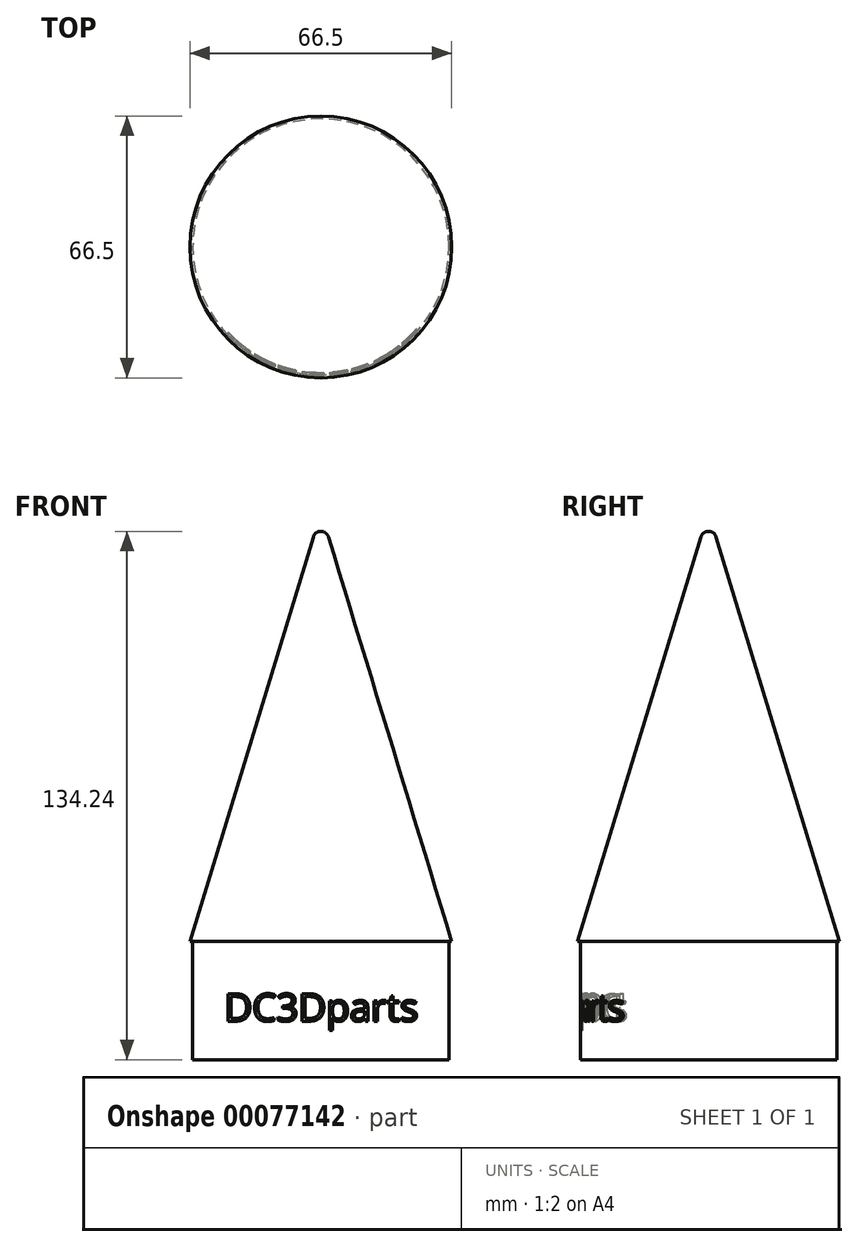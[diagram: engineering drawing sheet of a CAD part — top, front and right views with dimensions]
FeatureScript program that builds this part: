
annotation { "Feature Type Name" : "Feature", "Feature Type Description" : "" }
export const myFeature = defineFeature(function(context is Context, id is Id, definition is map)
    precondition{}
    {
        {
            var Q0;
            Q0=qCreatedBy(makeId("Front.planeOp"),FACE);
            var sketch = newSketch(context, id + "F0", { "sketchPlane" : qUnion([Q0])});
            skLineSegment(sketch, "E0", {"start": v(0, 91.38) * mm, "end": v(0, -88.55) * mm, "construction": true});
            skPoint(sketch, "E0.startSnap0", {"position": v(0, 78.7) * mm});
            skLineSegment(sketch, "E1", {"start": v(-62.51, 0) * mm, "end": v(-32.55, 0) * mm, "construction": true});
            skLineSegment(sketch, "E2.top", {"start": v(0, -30) * mm, "end": v(-32.55, -30) * mm});
            skLineSegment(sketch, "E2.left", {"start": v(0, 0) * mm, "end": v(0, -30) * mm});
            skLineSegment(sketch, "E2.right", {"start": v(-32.55, 0) * mm, "end": v(-32.55, -30) * mm});
            skLineSegment(sketch, "E3", {"start": v(0, 78.7) * mm, "end": v(0, -30) * mm});
            skLineSegment(sketch, "E4.trimOffspring", {"start": v(0, 0) * mm, "end": v(63.8, 0) * mm, "construction": true});
            skLineSegment(sketch, "E5", {"start": v(-33.25, 0) * mm, "end": v(-32.55, 0) * mm});
            skLineSegment(sketch, "E6", {"start": v(-33.25, 0) * mm, "end": v(-1.92, 102.82) * mm});
            skLineSegment(sketch, "E7", {"start": v(0, 104.24) * mm, "end": v(0, -30) * mm});
            skArc(sketch, "E8", {"start": v(0, 104.24) * mm, "mid": v(-1.2, 103.85) * mm, "end": v(-1.92, 102.82) * mm});
            skPoint(sketch, "E9.orphan", {"position": v(0, 109.12) * mm});
            skSolve(sketch);
        }
        {
            var Q0;
            {var subQ0=sQuery(id+"F0.wireOp",EDGE,"E2.top");Q0=makeQuery(id+"F0.imprint","IMPRINT",FACE,{"disambiguationData":[TD([[makeQuery(id+"F0.imprint","IMPRINT",EDGE,{"derivedFrom":subQ0}),-1.0]])]});}
            var Q1;
            Q1=sQuery(id+"F0.wireOp",EDGE,"E0");
            revolve(context, id + "F1", {"entities" : qUnion([Q0]), "axis" : qUnion([Q1]), "revolveType" : RevolveType.FULL});
        }
        {
            var Q0;
            Q0=qCreatedBy(makeId("Front.planeOp"),FACE);
            cPlane(context, id + "F2", {"entities" : qUnion([Q0]), "cplaneType" : CPlaneType.OFFSET, "offset" : 40 * mm, "width" : 150 * mm, "height" : 150 * mm});
        }
        {
            var Q0;
            Q0=qCreatedBy(id+"F2.planeOp",FACE);
            var sketch = newSketch(context, id + "F3", { "sketchPlane" : qUnion([Q0])});
            skText(sketch, "E10", { "text": "DC3Dparts", "fontName": "OpenSans-Regular.ttf"});
            const initialGuessF3  = {"E10": [-0.02452, -0.02022, 1, 0, 0.007]};
            skSetInitialGuess(sketch, initialGuessF3);
            skSolve(sketch);
        }
        {
            var Q0;
            Q0 = qSketchRegion(id + "F3", true);
            var Q1;
            Q1=qCreatedBy(makeId("Front.planeOp"),FACE);
            extrude(context, id + "F4", {"entities" : qUnion([Q0]), "endBound" : BoundingType.UP_TO_SURFACE, "oppositeDirection" : true, "depth" : 25 * mm, "endBoundEntityFace" : qUnion([Q1]), "offsetDistance" : 25 * mm});
        }
        {
            var Q0;
            Q0=qCreatedBy(makeId("Front.planeOp"),FACE);
            var sketch = newSketch(context, id + "F5", { "sketchPlane" : qUnion([Q0])});
            skLineSegment(sketch, "E11.bottom", {"start": v(0, -2.97) * mm, "end": v(-32, -2.97) * mm});
            skLineSegment(sketch, "E11.top", {"start": v(0, -33.64) * mm, "end": v(-32, -33.64) * mm});
            skLineSegment(sketch, "E11.left", {"start": v(0, -2.97) * mm, "end": v(0, -33.64) * mm});
            skLineSegment(sketch, "E11.right", {"start": v(-32, -2.97) * mm, "end": v(-32, -33.64) * mm});
            skSolve(sketch);
        }
        {
            var Q0;
            Q0=makeQuery(id+"F5.imprint","IMPRINT",FACE,{"disambiguationData":[TD([[makeQuery(id+"F5.imprint","IMPRINT",EDGE,{"derivedFrom":sQuery(id+"F5.wireOp",EDGE,"E11.bottom")}),1.0]])]});
            var Q1;
            Q1=sQuery(id+"F5.wireOp",EDGE,"E11.left");
            revolve(context, id + "F6", {"entities" : qUnion([Q0]), "axis" : qUnion([Q1]), "revolveType" : RevolveType.FULL});
        }
        {
            var Q0;
            Q0=makeQuery(id+"F6.opRevolve","SWEPT_BODY",BODY,{"disambiguationData":[OSD([sQuery(id+"F5.wireOp",EDGE,"E11.bottom"),sQuery(id+"F5.wireOp",EDGE,"E11.top"),sQuery(id+"F5.wireOp",EDGE,"E11.left"),sQuery(id+"F5.wireOp",EDGE,"E11.right")])]});
            var Q1;
            Q1=makeQuery(id+"F4.opExtrude","SWEPT_BODY",BODY,{"disambiguationData":[OSD([sQuery(id+"F3.wireOp",EDGE,"E10.sketch_text.stroke-0"),sQuery(id+"F3.wireOp",EDGE,"E10.sketch_text.stroke-1"),sQuery(id+"F3.wireOp",EDGE,"E10.sketch_text.stroke-2"),sQuery(id+"F3.wireOp",EDGE,"E10.sketch_text.stroke-3"),sQuery(id+"F3.wireOp",EDGE,"E10.sketch_text.stroke-4"),sQuery(id+"F3.wireOp",EDGE,"E10.sketch_text.stroke-5"),sQuery(id+"F3.wireOp",EDGE,"E10.sketch_text.stroke-6"),sQuery(id+"F3.wireOp",EDGE,"E10.sketch_text.stroke-7"),sQuery(id+"F3.wireOp",EDGE,"E10.sketch_text.stroke-8"),sQuery(id+"F3.wireOp",EDGE,"E10.sketch_text.stroke-9"),sQuery(id+"F3.wireOp",EDGE,"E10.sketch_text.stroke-10"),sQuery(id+"F3.wireOp",EDGE,"E10.sketch_text.stroke-11"),sQuery(id+"F3.wireOp",EDGE,"E10.sketch_text.stroke-12"),sQuery(id+"F3.wireOp",EDGE,"E10.sketch_text.stroke-13")])]});
            var Q2;
            Q2=makeQuery(id+"F4.opExtrude","SWEPT_BODY",BODY,{"disambiguationData":[OSD([sQuery(id+"F3.wireOp",EDGE,"E10.sketch_text.stroke-14"),sQuery(id+"F3.wireOp",EDGE,"E10.sketch_text.stroke-15"),sQuery(id+"F3.wireOp",EDGE,"E10.sketch_text.stroke-16"),sQuery(id+"F3.wireOp",EDGE,"E10.sketch_text.stroke-17"),sQuery(id+"F3.wireOp",EDGE,"E10.sketch_text.stroke-18"),sQuery(id+"F3.wireOp",EDGE,"E10.sketch_text.stroke-19"),sQuery(id+"F3.wireOp",EDGE,"E10.sketch_text.stroke-20"),sQuery(id+"F3.wireOp",EDGE,"E10.sketch_text.stroke-21"),sQuery(id+"F3.wireOp",EDGE,"E10.sketch_text.stroke-22"),sQuery(id+"F3.wireOp",EDGE,"E10.sketch_text.stroke-23"),sQuery(id+"F3.wireOp",EDGE,"E10.sketch_text.stroke-24"),sQuery(id+"F3.wireOp",EDGE,"E10.sketch_text.stroke-25"),sQuery(id+"F3.wireOp",EDGE,"E10.sketch_text.stroke-26"),sQuery(id+"F3.wireOp",EDGE,"E10.sketch_text.stroke-27"),sQuery(id+"F3.wireOp",EDGE,"E10.sketch_text.stroke-28")])]});
            var Q3;
            Q3=makeQuery(id+"F4.opExtrude","SWEPT_BODY",BODY,{"disambiguationData":[OSD([sQuery(id+"F3.wireOp",EDGE,"E10.sketch_text.stroke-29"),sQuery(id+"F3.wireOp",EDGE,"E10.sketch_text.stroke-30"),sQuery(id+"F3.wireOp",EDGE,"E10.sketch_text.stroke-31"),sQuery(id+"F3.wireOp",EDGE,"E10.sketch_text.stroke-32"),sQuery(id+"F3.wireOp",EDGE,"E10.sketch_text.stroke-33"),sQuery(id+"F3.wireOp",EDGE,"E10.sketch_text.stroke-34"),sQuery(id+"F3.wireOp",EDGE,"E10.sketch_text.stroke-35"),sQuery(id+"F3.wireOp",EDGE,"E10.sketch_text.stroke-36"),sQuery(id+"F3.wireOp",EDGE,"E10.sketch_text.stroke-37"),sQuery(id+"F3.wireOp",EDGE,"E10.sketch_text.stroke-38"),sQuery(id+"F3.wireOp",EDGE,"E10.sketch_text.stroke-39"),sQuery(id+"F3.wireOp",EDGE,"E10.sketch_text.stroke-40"),sQuery(id+"F3.wireOp",EDGE,"E10.sketch_text.stroke-41"),sQuery(id+"F3.wireOp",EDGE,"E10.sketch_text.stroke-42"),sQuery(id+"F3.wireOp",EDGE,"E10.sketch_text.stroke-43"),sQuery(id+"F3.wireOp",EDGE,"E10.sketch_text.stroke-44"),sQuery(id+"F3.wireOp",EDGE,"E10.sketch_text.stroke-45"),sQuery(id+"F3.wireOp",EDGE,"E10.sketch_text.stroke-46"),sQuery(id+"F3.wireOp",EDGE,"E10.sketch_text.stroke-47"),sQuery(id+"F3.wireOp",EDGE,"E10.sketch_text.stroke-48"),sQuery(id+"F3.wireOp",EDGE,"E10.sketch_text.stroke-49"),sQuery(id+"F3.wireOp",EDGE,"E10.sketch_text.stroke-50"),sQuery(id+"F3.wireOp",EDGE,"E10.sketch_text.stroke-51"),sQuery(id+"F3.wireOp",EDGE,"E10.sketch_text.stroke-52"),sQuery(id+"F3.wireOp",EDGE,"E10.sketch_text.stroke-53"),sQuery(id+"F3.wireOp",EDGE,"E10.sketch_text.stroke-54"),sQuery(id+"F3.wireOp",EDGE,"E10.sketch_text.stroke-55"),sQuery(id+"F3.wireOp",EDGE,"E10.sketch_text.stroke-56")])]});
            var Q4;
            Q4=makeQuery(id+"F4.opExtrude","SWEPT_BODY",BODY,{"disambiguationData":[OSD([sQuery(id+"F3.wireOp",EDGE,"E10.sketch_text.stroke-57"),sQuery(id+"F3.wireOp",EDGE,"E10.sketch_text.stroke-58"),sQuery(id+"F3.wireOp",EDGE,"E10.sketch_text.stroke-59"),sQuery(id+"F3.wireOp",EDGE,"E10.sketch_text.stroke-60"),sQuery(id+"F3.wireOp",EDGE,"E10.sketch_text.stroke-61"),sQuery(id+"F3.wireOp",EDGE,"E10.sketch_text.stroke-62"),sQuery(id+"F3.wireOp",EDGE,"E10.sketch_text.stroke-63"),sQuery(id+"F3.wireOp",EDGE,"E10.sketch_text.stroke-64"),sQuery(id+"F3.wireOp",EDGE,"E10.sketch_text.stroke-65"),sQuery(id+"F3.wireOp",EDGE,"E10.sketch_text.stroke-66"),sQuery(id+"F3.wireOp",EDGE,"E10.sketch_text.stroke-67"),sQuery(id+"F3.wireOp",EDGE,"E10.sketch_text.stroke-68"),sQuery(id+"F3.wireOp",EDGE,"E10.sketch_text.stroke-69"),sQuery(id+"F3.wireOp",EDGE,"E10.sketch_text.stroke-70")])]});
            var Q5;
            Q5=makeQuery(id+"F4.opExtrude","SWEPT_BODY",BODY,{"disambiguationData":[OSD([sQuery(id+"F3.wireOp",EDGE,"E10.sketch_text.stroke-71"),sQuery(id+"F3.wireOp",EDGE,"E10.sketch_text.stroke-72"),sQuery(id+"F3.wireOp",EDGE,"E10.sketch_text.stroke-73"),sQuery(id+"F3.wireOp",EDGE,"E10.sketch_text.stroke-74"),sQuery(id+"F3.wireOp",EDGE,"E10.sketch_text.stroke-75"),sQuery(id+"F3.wireOp",EDGE,"E10.sketch_text.stroke-76"),sQuery(id+"F3.wireOp",EDGE,"E10.sketch_text.stroke-77"),sQuery(id+"F3.wireOp",EDGE,"E10.sketch_text.stroke-78"),sQuery(id+"F3.wireOp",EDGE,"E10.sketch_text.stroke-79"),sQuery(id+"F3.wireOp",EDGE,"E10.sketch_text.stroke-80"),sQuery(id+"F3.wireOp",EDGE,"E10.sketch_text.stroke-81"),sQuery(id+"F3.wireOp",EDGE,"E10.sketch_text.stroke-82"),sQuery(id+"F3.wireOp",EDGE,"E10.sketch_text.stroke-83"),sQuery(id+"F3.wireOp",EDGE,"E10.sketch_text.stroke-84"),sQuery(id+"F3.wireOp",EDGE,"E10.sketch_text.stroke-85"),sQuery(id+"F3.wireOp",EDGE,"E10.sketch_text.stroke-86"),sQuery(id+"F3.wireOp",EDGE,"E10.sketch_text.stroke-87"),sQuery(id+"F3.wireOp",EDGE,"E10.sketch_text.stroke-88"),sQuery(id+"F3.wireOp",EDGE,"E10.sketch_text.stroke-89"),sQuery(id+"F3.wireOp",EDGE,"E10.sketch_text.stroke-90"),sQuery(id+"F3.wireOp",EDGE,"E10.sketch_text.stroke-91"),sQuery(id+"F3.wireOp",EDGE,"E10.sketch_text.stroke-92"),sQuery(id+"F3.wireOp",EDGE,"E10.sketch_text.stroke-93"),sQuery(id+"F3.wireOp",EDGE,"E10.sketch_text.stroke-94"),sQuery(id+"F3.wireOp",EDGE,"E10.sketch_text.stroke-95")])]});
            var Q6;
            Q6=makeQuery(id+"F4.opExtrude","SWEPT_BODY",BODY,{"disambiguationData":[OSD([sQuery(id+"F3.wireOp",EDGE,"E10.sketch_text.stroke-96"),sQuery(id+"F3.wireOp",EDGE,"E10.sketch_text.stroke-97"),sQuery(id+"F3.wireOp",EDGE,"E10.sketch_text.stroke-98"),sQuery(id+"F3.wireOp",EDGE,"E10.sketch_text.stroke-99"),sQuery(id+"F3.wireOp",EDGE,"E10.sketch_text.stroke-100"),sQuery(id+"F3.wireOp",EDGE,"E10.sketch_text.stroke-101"),sQuery(id+"F3.wireOp",EDGE,"E10.sketch_text.stroke-102"),sQuery(id+"F3.wireOp",EDGE,"E10.sketch_text.stroke-103"),sQuery(id+"F3.wireOp",EDGE,"E10.sketch_text.stroke-104"),sQuery(id+"F3.wireOp",EDGE,"E10.sketch_text.stroke-105"),sQuery(id+"F3.wireOp",EDGE,"E10.sketch_text.stroke-106"),sQuery(id+"F3.wireOp",EDGE,"E10.sketch_text.stroke-107"),sQuery(id+"F3.wireOp",EDGE,"E10.sketch_text.stroke-108"),sQuery(id+"F3.wireOp",EDGE,"E10.sketch_text.stroke-109"),sQuery(id+"F3.wireOp",EDGE,"E10.sketch_text.stroke-110"),sQuery(id+"F3.wireOp",EDGE,"E10.sketch_text.stroke-111"),sQuery(id+"F3.wireOp",EDGE,"E10.sketch_text.stroke-112"),sQuery(id+"F3.wireOp",EDGE,"E10.sketch_text.stroke-113"),sQuery(id+"F3.wireOp",EDGE,"E10.sketch_text.stroke-114"),sQuery(id+"F3.wireOp",EDGE,"E10.sketch_text.stroke-115"),sQuery(id+"F3.wireOp",EDGE,"E10.sketch_text.stroke-116"),sQuery(id+"F3.wireOp",EDGE,"E10.sketch_text.stroke-117"),sQuery(id+"F3.wireOp",EDGE,"E10.sketch_text.stroke-118"),sQuery(id+"F3.wireOp",EDGE,"E10.sketch_text.stroke-119"),sQuery(id+"F3.wireOp",EDGE,"E10.sketch_text.stroke-120"),sQuery(id+"F3.wireOp",EDGE,"E10.sketch_text.stroke-121"),sQuery(id+"F3.wireOp",EDGE,"E10.sketch_text.stroke-122")])]});
            var Q7;
            Q7=makeQuery(id+"F4.opExtrude","SWEPT_BODY",BODY,{"disambiguationData":[OSD([sQuery(id+"F3.wireOp",EDGE,"E10.sketch_text.stroke-123"),sQuery(id+"F3.wireOp",EDGE,"E10.sketch_text.stroke-124"),sQuery(id+"F3.wireOp",EDGE,"E10.sketch_text.stroke-125"),sQuery(id+"F3.wireOp",EDGE,"E10.sketch_text.stroke-126"),sQuery(id+"F3.wireOp",EDGE,"E10.sketch_text.stroke-127"),sQuery(id+"F3.wireOp",EDGE,"E10.sketch_text.stroke-128"),sQuery(id+"F3.wireOp",EDGE,"E10.sketch_text.stroke-129"),sQuery(id+"F3.wireOp",EDGE,"E10.sketch_text.stroke-130"),sQuery(id+"F3.wireOp",EDGE,"E10.sketch_text.stroke-131"),sQuery(id+"F3.wireOp",EDGE,"E10.sketch_text.stroke-132"),sQuery(id+"F3.wireOp",EDGE,"E10.sketch_text.stroke-133"),sQuery(id+"F3.wireOp",EDGE,"E10.sketch_text.stroke-134"),sQuery(id+"F3.wireOp",EDGE,"E10.sketch_text.stroke-135")])]});
            var Q8;
            Q8=makeQuery(id+"F4.opExtrude","SWEPT_BODY",BODY,{"disambiguationData":[OSD([sQuery(id+"F3.wireOp",EDGE,"E10.sketch_text.stroke-136"),sQuery(id+"F3.wireOp",EDGE,"E10.sketch_text.stroke-137"),sQuery(id+"F3.wireOp",EDGE,"E10.sketch_text.stroke-138"),sQuery(id+"F3.wireOp",EDGE,"E10.sketch_text.stroke-139"),sQuery(id+"F3.wireOp",EDGE,"E10.sketch_text.stroke-140"),sQuery(id+"F3.wireOp",EDGE,"E10.sketch_text.stroke-141"),sQuery(id+"F3.wireOp",EDGE,"E10.sketch_text.stroke-142"),sQuery(id+"F3.wireOp",EDGE,"E10.sketch_text.stroke-143"),sQuery(id+"F3.wireOp",EDGE,"E10.sketch_text.stroke-144"),sQuery(id+"F3.wireOp",EDGE,"E10.sketch_text.stroke-145"),sQuery(id+"F3.wireOp",EDGE,"E10.sketch_text.stroke-146"),sQuery(id+"F3.wireOp",EDGE,"E10.sketch_text.stroke-147"),sQuery(id+"F3.wireOp",EDGE,"E10.sketch_text.stroke-148"),sQuery(id+"F3.wireOp",EDGE,"E10.sketch_text.stroke-149"),sQuery(id+"F3.wireOp",EDGE,"E10.sketch_text.stroke-150"),sQuery(id+"F3.wireOp",EDGE,"E10.sketch_text.stroke-151"),sQuery(id+"F3.wireOp",EDGE,"E10.sketch_text.stroke-152"),sQuery(id+"F3.wireOp",EDGE,"E10.sketch_text.stroke-153"),sQuery(id+"F3.wireOp",EDGE,"E10.sketch_text.stroke-154")])]});
            var Q9;
            Q9=makeQuery(id+"F4.opExtrude","SWEPT_BODY",BODY,{"disambiguationData":[OSD([sQuery(id+"F3.wireOp",EDGE,"E10.sketch_text.stroke-155"),sQuery(id+"F3.wireOp",EDGE,"E10.sketch_text.stroke-156"),sQuery(id+"F3.wireOp",EDGE,"E10.sketch_text.stroke-157"),sQuery(id+"F3.wireOp",EDGE,"E10.sketch_text.stroke-158"),sQuery(id+"F3.wireOp",EDGE,"E10.sketch_text.stroke-159"),sQuery(id+"F3.wireOp",EDGE,"E10.sketch_text.stroke-160"),sQuery(id+"F3.wireOp",EDGE,"E10.sketch_text.stroke-161"),sQuery(id+"F3.wireOp",EDGE,"E10.sketch_text.stroke-162"),sQuery(id+"F3.wireOp",EDGE,"E10.sketch_text.stroke-163"),sQuery(id+"F3.wireOp",EDGE,"E10.sketch_text.stroke-164"),sQuery(id+"F3.wireOp",EDGE,"E10.sketch_text.stroke-165"),sQuery(id+"F3.wireOp",EDGE,"E10.sketch_text.stroke-166"),sQuery(id+"F3.wireOp",EDGE,"E10.sketch_text.stroke-167"),sQuery(id+"F3.wireOp",EDGE,"E10.sketch_text.stroke-168"),sQuery(id+"F3.wireOp",EDGE,"E10.sketch_text.stroke-169"),sQuery(id+"F3.wireOp",EDGE,"E10.sketch_text.stroke-170"),sQuery(id+"F3.wireOp",EDGE,"E10.sketch_text.stroke-171"),sQuery(id+"F3.wireOp",EDGE,"E10.sketch_text.stroke-172"),sQuery(id+"F3.wireOp",EDGE,"E10.sketch_text.stroke-173"),sQuery(id+"F3.wireOp",EDGE,"E10.sketch_text.stroke-174"),sQuery(id+"F3.wireOp",EDGE,"E10.sketch_text.stroke-175"),sQuery(id+"F3.wireOp",EDGE,"E10.sketch_text.stroke-176"),sQuery(id+"F3.wireOp",EDGE,"E10.sketch_text.stroke-177"),sQuery(id+"F3.wireOp",EDGE,"E10.sketch_text.stroke-178"),sQuery(id+"F3.wireOp",EDGE,"E10.sketch_text.stroke-179")])]});
            booleanBodies(context, id + "F7", {"operationType" : BooleanOperationType.SUBTRACTION, "tools" : qUnion([Q0]), "targets" : qUnion([Q1, Q2, Q3, Q4, Q5, Q6, Q7, Q8, Q9])});
        }
        {
            var Q0;
            Q0=makeQuery(id+"F4.opExtrude","SWEPT_BODY",BODY,{"disambiguationData":[OSD([sQuery(id+"F3.wireOp",EDGE,"E10.sketch_text.stroke-0"),sQuery(id+"F3.wireOp",EDGE,"E10.sketch_text.stroke-1"),sQuery(id+"F3.wireOp",EDGE,"E10.sketch_text.stroke-2"),sQuery(id+"F3.wireOp",EDGE,"E10.sketch_text.stroke-3"),sQuery(id+"F3.wireOp",EDGE,"E10.sketch_text.stroke-4"),sQuery(id+"F3.wireOp",EDGE,"E10.sketch_text.stroke-5"),sQuery(id+"F3.wireOp",EDGE,"E10.sketch_text.stroke-6"),sQuery(id+"F3.wireOp",EDGE,"E10.sketch_text.stroke-7"),sQuery(id+"F3.wireOp",EDGE,"E10.sketch_text.stroke-8"),sQuery(id+"F3.wireOp",EDGE,"E10.sketch_text.stroke-9"),sQuery(id+"F3.wireOp",EDGE,"E10.sketch_text.stroke-10"),sQuery(id+"F3.wireOp",EDGE,"E10.sketch_text.stroke-11"),sQuery(id+"F3.wireOp",EDGE,"E10.sketch_text.stroke-12"),sQuery(id+"F3.wireOp",EDGE,"E10.sketch_text.stroke-13")])]});
            var Q1;
            Q1=makeQuery(id+"F4.opExtrude","SWEPT_BODY",BODY,{"disambiguationData":[OSD([sQuery(id+"F3.wireOp",EDGE,"E10.sketch_text.stroke-14"),sQuery(id+"F3.wireOp",EDGE,"E10.sketch_text.stroke-15"),sQuery(id+"F3.wireOp",EDGE,"E10.sketch_text.stroke-16"),sQuery(id+"F3.wireOp",EDGE,"E10.sketch_text.stroke-17"),sQuery(id+"F3.wireOp",EDGE,"E10.sketch_text.stroke-18"),sQuery(id+"F3.wireOp",EDGE,"E10.sketch_text.stroke-19"),sQuery(id+"F3.wireOp",EDGE,"E10.sketch_text.stroke-20"),sQuery(id+"F3.wireOp",EDGE,"E10.sketch_text.stroke-21"),sQuery(id+"F3.wireOp",EDGE,"E10.sketch_text.stroke-22"),sQuery(id+"F3.wireOp",EDGE,"E10.sketch_text.stroke-23"),sQuery(id+"F3.wireOp",EDGE,"E10.sketch_text.stroke-24"),sQuery(id+"F3.wireOp",EDGE,"E10.sketch_text.stroke-25"),sQuery(id+"F3.wireOp",EDGE,"E10.sketch_text.stroke-26"),sQuery(id+"F3.wireOp",EDGE,"E10.sketch_text.stroke-27"),sQuery(id+"F3.wireOp",EDGE,"E10.sketch_text.stroke-28")])]});
            var Q2;
            Q2=makeQuery(id+"F4.opExtrude","SWEPT_BODY",BODY,{"disambiguationData":[OSD([sQuery(id+"F3.wireOp",EDGE,"E10.sketch_text.stroke-29"),sQuery(id+"F3.wireOp",EDGE,"E10.sketch_text.stroke-30"),sQuery(id+"F3.wireOp",EDGE,"E10.sketch_text.stroke-31"),sQuery(id+"F3.wireOp",EDGE,"E10.sketch_text.stroke-32"),sQuery(id+"F3.wireOp",EDGE,"E10.sketch_text.stroke-33"),sQuery(id+"F3.wireOp",EDGE,"E10.sketch_text.stroke-34"),sQuery(id+"F3.wireOp",EDGE,"E10.sketch_text.stroke-35"),sQuery(id+"F3.wireOp",EDGE,"E10.sketch_text.stroke-36"),sQuery(id+"F3.wireOp",EDGE,"E10.sketch_text.stroke-37"),sQuery(id+"F3.wireOp",EDGE,"E10.sketch_text.stroke-38"),sQuery(id+"F3.wireOp",EDGE,"E10.sketch_text.stroke-39"),sQuery(id+"F3.wireOp",EDGE,"E10.sketch_text.stroke-40"),sQuery(id+"F3.wireOp",EDGE,"E10.sketch_text.stroke-41"),sQuery(id+"F3.wireOp",EDGE,"E10.sketch_text.stroke-42"),sQuery(id+"F3.wireOp",EDGE,"E10.sketch_text.stroke-43"),sQuery(id+"F3.wireOp",EDGE,"E10.sketch_text.stroke-44"),sQuery(id+"F3.wireOp",EDGE,"E10.sketch_text.stroke-45"),sQuery(id+"F3.wireOp",EDGE,"E10.sketch_text.stroke-46"),sQuery(id+"F3.wireOp",EDGE,"E10.sketch_text.stroke-47"),sQuery(id+"F3.wireOp",EDGE,"E10.sketch_text.stroke-48"),sQuery(id+"F3.wireOp",EDGE,"E10.sketch_text.stroke-49"),sQuery(id+"F3.wireOp",EDGE,"E10.sketch_text.stroke-50"),sQuery(id+"F3.wireOp",EDGE,"E10.sketch_text.stroke-51"),sQuery(id+"F3.wireOp",EDGE,"E10.sketch_text.stroke-52"),sQuery(id+"F3.wireOp",EDGE,"E10.sketch_text.stroke-53"),sQuery(id+"F3.wireOp",EDGE,"E10.sketch_text.stroke-54"),sQuery(id+"F3.wireOp",EDGE,"E10.sketch_text.stroke-55"),sQuery(id+"F3.wireOp",EDGE,"E10.sketch_text.stroke-56")])]});
            var Q3;
            Q3=makeQuery(id+"F4.opExtrude","SWEPT_BODY",BODY,{"disambiguationData":[OSD([sQuery(id+"F3.wireOp",EDGE,"E10.sketch_text.stroke-57"),sQuery(id+"F3.wireOp",EDGE,"E10.sketch_text.stroke-58"),sQuery(id+"F3.wireOp",EDGE,"E10.sketch_text.stroke-59"),sQuery(id+"F3.wireOp",EDGE,"E10.sketch_text.stroke-60"),sQuery(id+"F3.wireOp",EDGE,"E10.sketch_text.stroke-61"),sQuery(id+"F3.wireOp",EDGE,"E10.sketch_text.stroke-62"),sQuery(id+"F3.wireOp",EDGE,"E10.sketch_text.stroke-63"),sQuery(id+"F3.wireOp",EDGE,"E10.sketch_text.stroke-64"),sQuery(id+"F3.wireOp",EDGE,"E10.sketch_text.stroke-65"),sQuery(id+"F3.wireOp",EDGE,"E10.sketch_text.stroke-66"),sQuery(id+"F3.wireOp",EDGE,"E10.sketch_text.stroke-67"),sQuery(id+"F3.wireOp",EDGE,"E10.sketch_text.stroke-68"),sQuery(id+"F3.wireOp",EDGE,"E10.sketch_text.stroke-69"),sQuery(id+"F3.wireOp",EDGE,"E10.sketch_text.stroke-70")])]});
            var Q4;
            Q4=makeQuery(id+"F4.opExtrude","SWEPT_BODY",BODY,{"disambiguationData":[OSD([sQuery(id+"F3.wireOp",EDGE,"E10.sketch_text.stroke-71"),sQuery(id+"F3.wireOp",EDGE,"E10.sketch_text.stroke-72"),sQuery(id+"F3.wireOp",EDGE,"E10.sketch_text.stroke-73"),sQuery(id+"F3.wireOp",EDGE,"E10.sketch_text.stroke-74"),sQuery(id+"F3.wireOp",EDGE,"E10.sketch_text.stroke-75"),sQuery(id+"F3.wireOp",EDGE,"E10.sketch_text.stroke-76"),sQuery(id+"F3.wireOp",EDGE,"E10.sketch_text.stroke-77"),sQuery(id+"F3.wireOp",EDGE,"E10.sketch_text.stroke-78"),sQuery(id+"F3.wireOp",EDGE,"E10.sketch_text.stroke-79"),sQuery(id+"F3.wireOp",EDGE,"E10.sketch_text.stroke-80"),sQuery(id+"F3.wireOp",EDGE,"E10.sketch_text.stroke-81"),sQuery(id+"F3.wireOp",EDGE,"E10.sketch_text.stroke-82"),sQuery(id+"F3.wireOp",EDGE,"E10.sketch_text.stroke-83"),sQuery(id+"F3.wireOp",EDGE,"E10.sketch_text.stroke-84"),sQuery(id+"F3.wireOp",EDGE,"E10.sketch_text.stroke-85"),sQuery(id+"F3.wireOp",EDGE,"E10.sketch_text.stroke-86"),sQuery(id+"F3.wireOp",EDGE,"E10.sketch_text.stroke-87"),sQuery(id+"F3.wireOp",EDGE,"E10.sketch_text.stroke-88"),sQuery(id+"F3.wireOp",EDGE,"E10.sketch_text.stroke-89"),sQuery(id+"F3.wireOp",EDGE,"E10.sketch_text.stroke-90"),sQuery(id+"F3.wireOp",EDGE,"E10.sketch_text.stroke-91"),sQuery(id+"F3.wireOp",EDGE,"E10.sketch_text.stroke-92"),sQuery(id+"F3.wireOp",EDGE,"E10.sketch_text.stroke-93"),sQuery(id+"F3.wireOp",EDGE,"E10.sketch_text.stroke-94"),sQuery(id+"F3.wireOp",EDGE,"E10.sketch_text.stroke-95")])]});
            var Q5;
            Q5=makeQuery(id+"F4.opExtrude","SWEPT_BODY",BODY,{"disambiguationData":[OSD([sQuery(id+"F3.wireOp",EDGE,"E10.sketch_text.stroke-96"),sQuery(id+"F3.wireOp",EDGE,"E10.sketch_text.stroke-97"),sQuery(id+"F3.wireOp",EDGE,"E10.sketch_text.stroke-98"),sQuery(id+"F3.wireOp",EDGE,"E10.sketch_text.stroke-99"),sQuery(id+"F3.wireOp",EDGE,"E10.sketch_text.stroke-100"),sQuery(id+"F3.wireOp",EDGE,"E10.sketch_text.stroke-101"),sQuery(id+"F3.wireOp",EDGE,"E10.sketch_text.stroke-102"),sQuery(id+"F3.wireOp",EDGE,"E10.sketch_text.stroke-103"),sQuery(id+"F3.wireOp",EDGE,"E10.sketch_text.stroke-104"),sQuery(id+"F3.wireOp",EDGE,"E10.sketch_text.stroke-105"),sQuery(id+"F3.wireOp",EDGE,"E10.sketch_text.stroke-106"),sQuery(id+"F3.wireOp",EDGE,"E10.sketch_text.stroke-107"),sQuery(id+"F3.wireOp",EDGE,"E10.sketch_text.stroke-108"),sQuery(id+"F3.wireOp",EDGE,"E10.sketch_text.stroke-109"),sQuery(id+"F3.wireOp",EDGE,"E10.sketch_text.stroke-110"),sQuery(id+"F3.wireOp",EDGE,"E10.sketch_text.stroke-111"),sQuery(id+"F3.wireOp",EDGE,"E10.sketch_text.stroke-112"),sQuery(id+"F3.wireOp",EDGE,"E10.sketch_text.stroke-113"),sQuery(id+"F3.wireOp",EDGE,"E10.sketch_text.stroke-114"),sQuery(id+"F3.wireOp",EDGE,"E10.sketch_text.stroke-115"),sQuery(id+"F3.wireOp",EDGE,"E10.sketch_text.stroke-116"),sQuery(id+"F3.wireOp",EDGE,"E10.sketch_text.stroke-117"),sQuery(id+"F3.wireOp",EDGE,"E10.sketch_text.stroke-118"),sQuery(id+"F3.wireOp",EDGE,"E10.sketch_text.stroke-119"),sQuery(id+"F3.wireOp",EDGE,"E10.sketch_text.stroke-120"),sQuery(id+"F3.wireOp",EDGE,"E10.sketch_text.stroke-121"),sQuery(id+"F3.wireOp",EDGE,"E10.sketch_text.stroke-122")])]});
            var Q6;
            Q6=makeQuery(id+"F4.opExtrude","SWEPT_BODY",BODY,{"disambiguationData":[OSD([sQuery(id+"F3.wireOp",EDGE,"E10.sketch_text.stroke-123"),sQuery(id+"F3.wireOp",EDGE,"E10.sketch_text.stroke-124"),sQuery(id+"F3.wireOp",EDGE,"E10.sketch_text.stroke-125"),sQuery(id+"F3.wireOp",EDGE,"E10.sketch_text.stroke-126"),sQuery(id+"F3.wireOp",EDGE,"E10.sketch_text.stroke-127"),sQuery(id+"F3.wireOp",EDGE,"E10.sketch_text.stroke-128"),sQuery(id+"F3.wireOp",EDGE,"E10.sketch_text.stroke-129"),sQuery(id+"F3.wireOp",EDGE,"E10.sketch_text.stroke-130"),sQuery(id+"F3.wireOp",EDGE,"E10.sketch_text.stroke-131"),sQuery(id+"F3.wireOp",EDGE,"E10.sketch_text.stroke-132"),sQuery(id+"F3.wireOp",EDGE,"E10.sketch_text.stroke-133"),sQuery(id+"F3.wireOp",EDGE,"E10.sketch_text.stroke-134"),sQuery(id+"F3.wireOp",EDGE,"E10.sketch_text.stroke-135")])]});
            var Q7;
            Q7=makeQuery(id+"F4.opExtrude","SWEPT_BODY",BODY,{"disambiguationData":[OSD([sQuery(id+"F3.wireOp",EDGE,"E10.sketch_text.stroke-136"),sQuery(id+"F3.wireOp",EDGE,"E10.sketch_text.stroke-137"),sQuery(id+"F3.wireOp",EDGE,"E10.sketch_text.stroke-138"),sQuery(id+"F3.wireOp",EDGE,"E10.sketch_text.stroke-139"),sQuery(id+"F3.wireOp",EDGE,"E10.sketch_text.stroke-140"),sQuery(id+"F3.wireOp",EDGE,"E10.sketch_text.stroke-141"),sQuery(id+"F3.wireOp",EDGE,"E10.sketch_text.stroke-142"),sQuery(id+"F3.wireOp",EDGE,"E10.sketch_text.stroke-143"),sQuery(id+"F3.wireOp",EDGE,"E10.sketch_text.stroke-144"),sQuery(id+"F3.wireOp",EDGE,"E10.sketch_text.stroke-145"),sQuery(id+"F3.wireOp",EDGE,"E10.sketch_text.stroke-146"),sQuery(id+"F3.wireOp",EDGE,"E10.sketch_text.stroke-147"),sQuery(id+"F3.wireOp",EDGE,"E10.sketch_text.stroke-148"),sQuery(id+"F3.wireOp",EDGE,"E10.sketch_text.stroke-149"),sQuery(id+"F3.wireOp",EDGE,"E10.sketch_text.stroke-150"),sQuery(id+"F3.wireOp",EDGE,"E10.sketch_text.stroke-151"),sQuery(id+"F3.wireOp",EDGE,"E10.sketch_text.stroke-152"),sQuery(id+"F3.wireOp",EDGE,"E10.sketch_text.stroke-153"),sQuery(id+"F3.wireOp",EDGE,"E10.sketch_text.stroke-154")])]});
            var Q8;
            Q8=makeQuery(id+"F4.opExtrude","SWEPT_BODY",BODY,{"disambiguationData":[OSD([sQuery(id+"F3.wireOp",EDGE,"E10.sketch_text.stroke-155"),sQuery(id+"F3.wireOp",EDGE,"E10.sketch_text.stroke-156"),sQuery(id+"F3.wireOp",EDGE,"E10.sketch_text.stroke-157"),sQuery(id+"F3.wireOp",EDGE,"E10.sketch_text.stroke-158"),sQuery(id+"F3.wireOp",EDGE,"E10.sketch_text.stroke-159"),sQuery(id+"F3.wireOp",EDGE,"E10.sketch_text.stroke-160"),sQuery(id+"F3.wireOp",EDGE,"E10.sketch_text.stroke-161"),sQuery(id+"F3.wireOp",EDGE,"E10.sketch_text.stroke-162"),sQuery(id+"F3.wireOp",EDGE,"E10.sketch_text.stroke-163"),sQuery(id+"F3.wireOp",EDGE,"E10.sketch_text.stroke-164"),sQuery(id+"F3.wireOp",EDGE,"E10.sketch_text.stroke-165"),sQuery(id+"F3.wireOp",EDGE,"E10.sketch_text.stroke-166"),sQuery(id+"F3.wireOp",EDGE,"E10.sketch_text.stroke-167"),sQuery(id+"F3.wireOp",EDGE,"E10.sketch_text.stroke-168"),sQuery(id+"F3.wireOp",EDGE,"E10.sketch_text.stroke-169"),sQuery(id+"F3.wireOp",EDGE,"E10.sketch_text.stroke-170"),sQuery(id+"F3.wireOp",EDGE,"E10.sketch_text.stroke-171"),sQuery(id+"F3.wireOp",EDGE,"E10.sketch_text.stroke-172"),sQuery(id+"F3.wireOp",EDGE,"E10.sketch_text.stroke-173"),sQuery(id+"F3.wireOp",EDGE,"E10.sketch_text.stroke-174"),sQuery(id+"F3.wireOp",EDGE,"E10.sketch_text.stroke-175"),sQuery(id+"F3.wireOp",EDGE,"E10.sketch_text.stroke-176"),sQuery(id+"F3.wireOp",EDGE,"E10.sketch_text.stroke-177"),sQuery(id+"F3.wireOp",EDGE,"E10.sketch_text.stroke-178"),sQuery(id+"F3.wireOp",EDGE,"E10.sketch_text.stroke-179")])]});
            var Q9;
            Q9=makeQuery(id+"F1.opRevolve","SWEPT_BODY",BODY,{"disambiguationData":[OSD([sQuery(id+"F0.wireOp",EDGE,"E2.top"),sQuery(id+"F0.wireOp",EDGE,"E2.right"),sQuery(id+"F0.wireOp",EDGE,"E5"),sQuery(id+"F0.wireOp",EDGE,"E6"),sQuery(id+"F0.wireOp",EDGE,"E7"),sQuery(id+"F0.wireOp",EDGE,"E8")])]});
            booleanBodies(context, id + "F8", {"operationType" : BooleanOperationType.SUBTRACTION, "tools" : qUnion([Q0, Q1, Q2, Q3, Q4, Q5, Q6, Q7, Q8]), "targets" : qUnion([Q9])});
        }
    });
